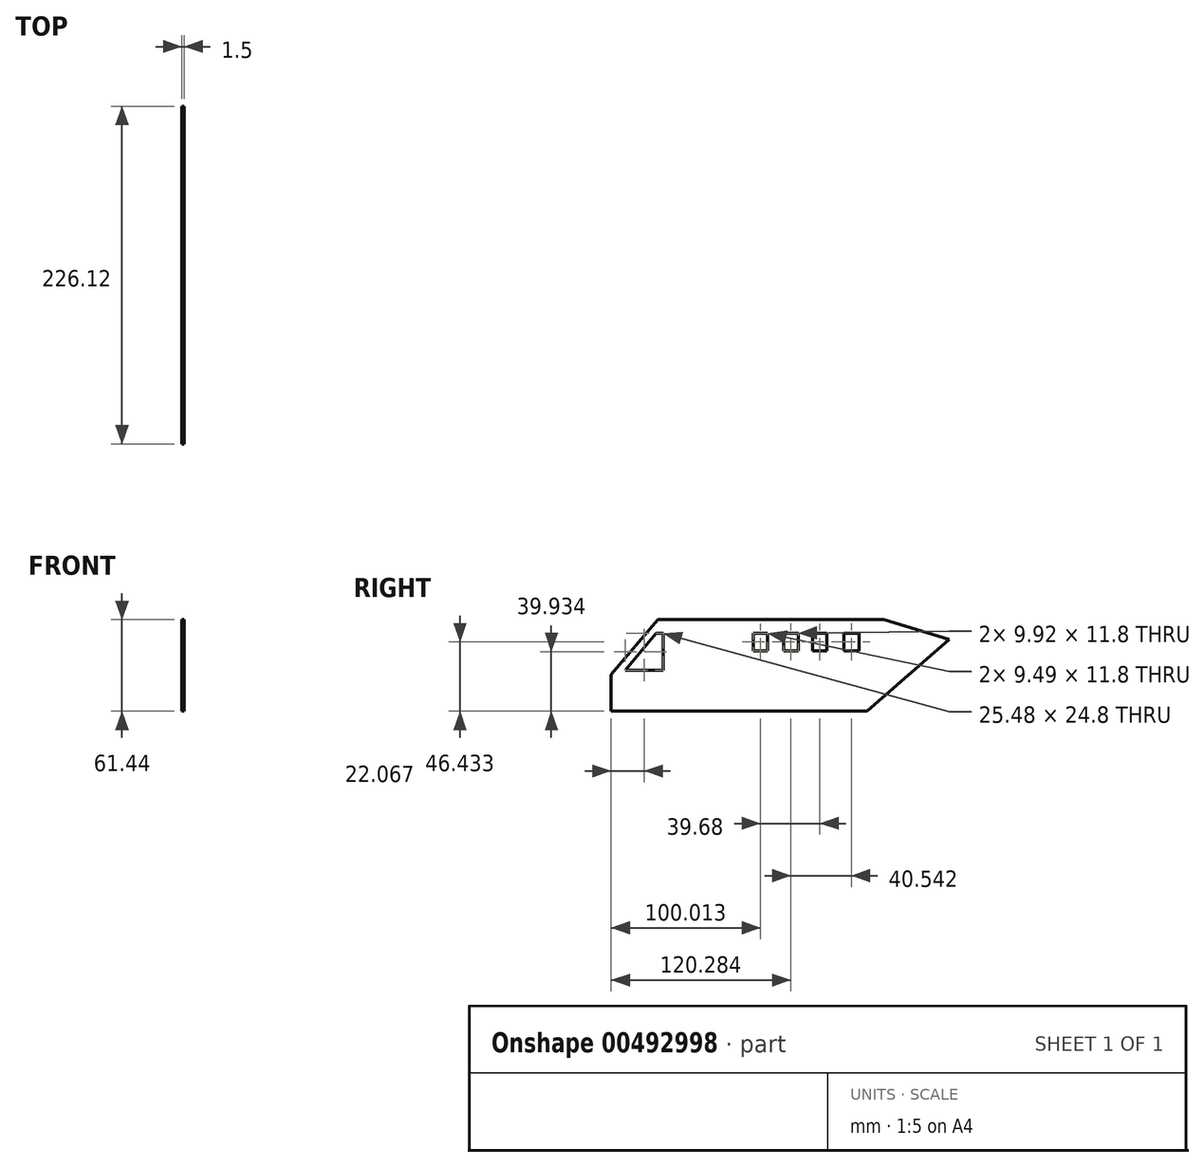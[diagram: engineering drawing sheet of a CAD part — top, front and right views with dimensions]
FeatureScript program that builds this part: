
annotation { "Feature Type Name" : "Feature", "Feature Type Description" : "" }
export const myFeature = defineFeature(function(context is Context, id is Id, definition is map)
    precondition{}
    {
        {
            var Q0;
            Q0=qCreatedBy(makeId("Right.planeOp"),FACE);
            var sketch = newSketch(context, id + "F0", { "sketchPlane" : qUnion([Q0])});
            skLineSegment(sketch, "E0", {"start": v(-80.23, -33.97) * mm, "end": v(90.94, -33.97) * mm});
            skLineSegment(sketch, "E1", {"start": v(90.94, -33.97) * mm, "end": v(145.9, 14.25) * mm});
            skLineSegment(sketch, "E2", {"start": v(145.9, 14.25) * mm, "end": v(102.1, 27.47) * mm});
            skLineSegment(sketch, "E3", {"start": v(102.1, 27.47) * mm, "end": v(-48.83, 27.47) * mm});
            skLineSegment(sketch, "E4", {"start": v(-80.23, -33.97) * mm, "end": v(-80.23, -9.4) * mm});
            skLineSegment(sketch, "E5", {"start": v(-80.23, -9.4) * mm, "end": v(-48.83, 27.47) * mm});
            skSolve(sketch);
        }
        {
            var Q0;
            Q0=qSketchRegion(id+"F0",true);
            extrude(context, id + "F1", {"entities" : qUnion([Q0]), "depth" : 1.5 * mm});
        }
        {
            var Q0;
            Q0=makeQuery(id+"F1.opExtrude","CAP_FACE",FACE,{"disambiguationData":[OSD([sQuery(id+"F0.wireOp",EDGE,"E0"),sQuery(id+"F0.wireOp",EDGE,"E1"),sQuery(id+"F0.wireOp",EDGE,"E2"),sQuery(id+"F0.wireOp",EDGE,"E3"),sQuery(id+"F0.wireOp",EDGE,"E4"),sQuery(id+"F0.wireOp",EDGE,"E5")])],"isStart":false});
            var sketch = newSketch(context, id + "F2", { "sketchPlane" : qUnion([Q0])});
            skLineSegment(sketch, "E6", {"start": v(-70.9, -6.44) * mm, "end": v(-45.42, -6.44) * mm});
            skLineSegment(sketch, "E7", {"start": v(-70.9, -6.44) * mm, "end": v(-50.2, 18.36) * mm});
            skLineSegment(sketch, "E8", {"start": v(-45.42, -6.44) * mm, "end": v(-45.42, 18.36) * mm});
            skLineSegment(sketch, "E9", {"start": v(-45.42, 18.36) * mm, "end": v(-50.2, 18.36) * mm});
            skPoint(sketch, "E10.startSnap0", {"position": v(-47.81, 18.36) * mm});
            skLineSegment(sketch, "E11", {"start": v(15.04, 18.36) * mm, "end": v(24.53, 18.36) * mm});
            skLineSegment(sketch, "E12", {"start": v(35.1, 18.36) * mm, "end": v(45.01, 18.36) * mm});
            skLineSegment(sketch, "E13", {"start": v(54.72, 18.36) * mm, "end": v(64.2, 18.36) * mm});
            skLineSegment(sketch, "E14", {"start": v(75.64, 18.36) * mm, "end": v(85.56, 18.36) * mm});
            skLineSegment(sketch, "E15", {"start": v(85.56, 18.36) * mm, "end": v(85.56, 6.56) * mm});
            skLineSegment(sketch, "E16", {"start": v(75.64, 18.36) * mm, "end": v(75.64, 6.56) * mm});
            skLineSegment(sketch, "E17", {"start": v(64.2, 18.36) * mm, "end": v(64.2, 6.56) * mm});
            skLineSegment(sketch, "E18", {"start": v(54.72, 18.36) * mm, "end": v(54.72, 6.56) * mm});
            skLineSegment(sketch, "E19", {"start": v(15.04, 18.36) * mm, "end": v(15.04, 6.56) * mm});
            skLineSegment(sketch, "E20", {"start": v(24.53, 18.36) * mm, "end": v(24.53, 6.56) * mm});
            skLineSegment(sketch, "E21", {"start": v(35.1, 18.36) * mm, "end": v(35.1, 6.56) * mm});
            skLineSegment(sketch, "E22", {"start": v(45.01, 18.36) * mm, "end": v(45.01, 6.56) * mm});
            skLineSegment(sketch, "E23", {"start": v(15.04, 6.56) * mm, "end": v(24.53, 6.56) * mm});
            skLineSegment(sketch, "E24", {"start": v(35.1, 6.56) * mm, "end": v(45.01, 6.56) * mm});
            skLineSegment(sketch, "E25", {"start": v(54.72, 6.56) * mm, "end": v(64.2, 6.56) * mm});
            skLineSegment(sketch, "E26", {"start": v(75.64, 6.56) * mm, "end": v(85.56, 6.56) * mm});
            skSolve(sketch);
        }
        {
            var Q0;
            Q0=qSketchRegion(id+"F2",true);
            extrude(context, id + "F3", {"entities" : qUnion([Q0]), "operationType" : NewBodyOperationType.REMOVE, "oppositeDirection" : true, "depth" : 1.5 * mm});
        }
    });
